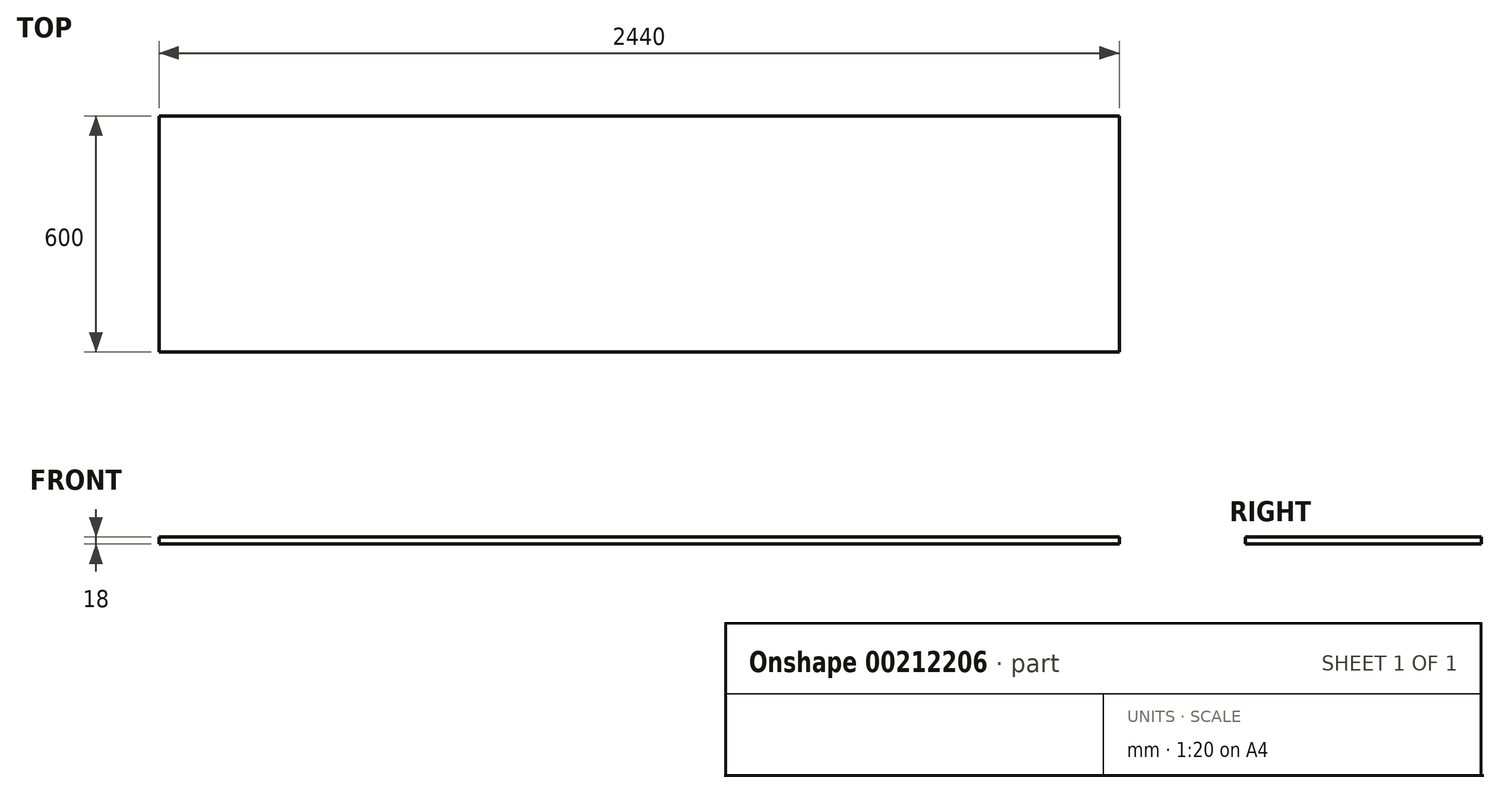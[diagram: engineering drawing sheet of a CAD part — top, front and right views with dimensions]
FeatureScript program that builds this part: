
annotation { "Feature Type Name" : "Feature", "Feature Type Description" : "" }
export const myFeature = defineFeature(function(context is Context, id is Id, definition is map)
    precondition{}
    {
        {
            var Q0;
            Q0=qCreatedBy(makeId("Top.planeOp"),FACE);
            var sketch = newSketch(context, id + "F0", { "sketchPlane" : qUnion([Q0])});
            skLineSegment(sketch, "E0.bottom", {"start": v(-1101.8, -182.55) * mm, "end": v(1338.2, -182.55) * mm});
            skLineSegment(sketch, "E0.top", {"start": v(-1101.8, -782.55) * mm, "end": v(1338.2, -782.55) * mm});
            skLineSegment(sketch, "E0.left", {"start": v(-1101.8, -182.55) * mm, "end": v(-1101.8, -782.55) * mm});
            skLineSegment(sketch, "E0.right", {"start": v(1338.2, -182.55) * mm, "end": v(1338.2, -782.55) * mm});
            skSolve(sketch);
        }
        {
            var Q0;
            Q0=makeQuery(id+"F0.imprint","IMPRINT",FACE,{"disambiguationData":[TD([[makeQuery(id+"F0.imprint","IMPRINT",EDGE,{"derivedFrom":sQuery(id+"F0.wireOp",EDGE,"E0.bottom")}),-1.0]])]});
            extrude(context, id + "F1", {"entities" : qUnion([Q0]), "depth" : 18 * mm});
        }
    });
